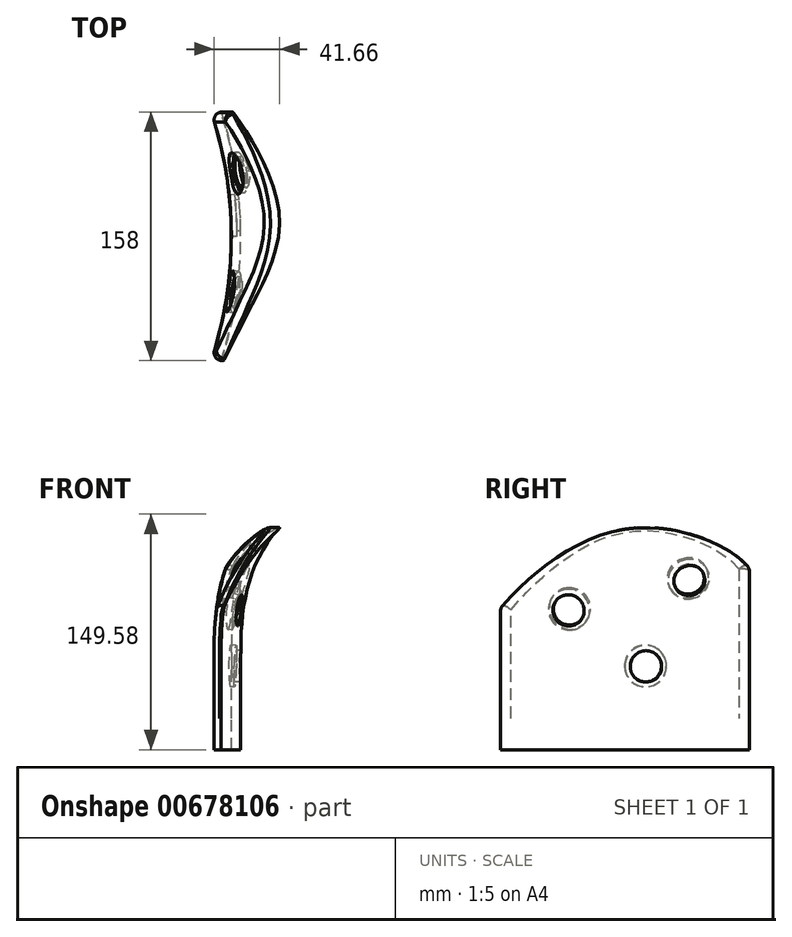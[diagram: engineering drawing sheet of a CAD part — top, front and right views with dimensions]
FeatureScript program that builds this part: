
annotation { "Feature Type Name" : "Feature", "Feature Type Description" : "" }
export const myFeature = defineFeature(function(context is Context, id is Id, definition is map)
    precondition{}
    {
        {
            var Q0;
            Q0=qCreatedBy(makeId("Top.planeOp"),FACE);
            var sketch = newSketch(context, id + "F0", { "sketchPlane" : qUnion([Q0])});
            skCircle(sketch, "E0", {"center": v(0, 0) * mm, "radius": 250 * mm});
            skCircle(sketch, "E1", {"center": v(0, 0) * mm, "radius": 256 * mm});
            skLineSegment(sketch, "E2", {"start": v(0, 0) * mm, "end": v(243.5, 79) * mm});
            skLineSegment(sketch, "E3", {"start": v(0, 0) * mm, "end": v(243.5, -79) * mm});
            skLineSegment(sketch, "E4", {"start": v(243.5, -79) * mm, "end": v(243.5, 79) * mm, "construction": true});
            skPoint(sketch, "E5", {"position": v(250, 0) * mm});
            skLineSegment(sketch, "E6", {"start": v(0, 0) * mm, "end": v(294.47, 0) * mm, "construction": true});
            skPoint(sketch, "E6.endSnap0", {"position": v(243.5, 0) * mm});
            skLineSegment(sketch, "E7", {"start": v(0, 0) * mm, "end": v(292.87, 46.39) * mm, "construction": true});
            skLineSegment(sketch, "E8", {"start": v(0, 0) * mm, "end": v(283.31, -39.82) * mm, "construction": true});
            skLineSegment(sketch, "E9", {"start": v(0, 0) * mm, "end": v(294.63, 15.44) * mm, "construction": true});
            skLineSegment(sketch, "E10", {"start": v(0, 0) * mm, "end": v(29.15, 207.44) * mm, "construction": true});
            skLineSegment(sketch, "E11", {"start": v(0, 0) * mm, "end": v(-10.87, 207.44) * mm, "construction": true});
            skLineSegment(sketch, "E12", {"start": v(0, 0) * mm, "end": v(-32.13, 202.88) * mm, "construction": true});
            skSolve(sketch);
        }
        {
            var Q0;
            Q0=qCreatedBy(makeId("Front.planeOp"),FACE);
            var sketch = newSketch(context, id + "F1", { "sketchPlane" : qUnion([Q0])});
            skLineSegment(sketch, "E13.0", {"start": v(-250, 0) * mm, "end": v(250, 0) * mm, "construction": true});
            skLineSegment(sketch, "E14.0", {"start": v(-256, 0) * mm, "end": v(256, 0) * mm, "construction": true});
            skPoint(sketch, "E15.0", {"position": v(243.5, 0) * mm});
            skLineSegment(sketch, "E16", {"start": v(250, 0) * mm, "end": v(256, 0) * mm, "construction": true});
            skPoint(sketch, "E17", {"position": v(253, 0) * mm});
            skFitSpline(sketch, "E18", {"points": [v(253, 0) * mm, v(253, 39.53) * mm, v(283, 127) * mm], "startDerivative": vector(0, 189.9) * mm, "endDerivative": vector(148.85, 126.61) * mm});
            skLineSegment(sketch, "E19", {"start": v(253, 0) * mm, "end": v(253, 133.7) * mm, "construction": true});
            skPoint(sketch, "E20", {"position": v(253, 66.85) * mm});
            skLineSegment(sketch, "E21", {"start": v(0, 0) * mm, "end": v(0, 247.7) * mm, "construction": true});
            skLineSegment(sketch, "E22", {"start": v(259.56, 90.88) * mm, "end": v(-13.45, 209.23) * mm, "construction": true});
            skLineSegment(sketch, "E23", {"start": v(0, 0) * mm, "end": v(70.48, 216.9) * mm, "construction": true});
            skLineSegment(sketch, "E24", {"start": v(0, 0) * mm, "end": v(46.92, 220.76) * mm, "construction": true});
            skLineSegment(sketch, "E25", {"start": v(0, 0) * mm, "end": v(14.68, 336.23) * mm, "construction": true});
            skSolve(sketch);
        }
        {
            var Q0;
            {var subQ0=sQuery(id+"F0.wireOp",EDGE,"E2");var subQ1=sQuery(id+"F0.wireOp",EDGE,"E0");var subQ2=makeQuery(id+"F0.imprint","INTERSECT",VERTEX,{"derivedFrom":[subQ1,subQ0]});Q0=makeQuery(id+"F0.imprint","IMPRINT",FACE,{"disambiguationData":[TD([[makeQuery(id+"F0.imprint","IMPRINT",EDGE,{"disambiguationData":[TD([[subQ2,1.0]])],"derivedFrom":subQ1}),-1.0]])]});}
            var Q1;
            Q1=sQuery(id+"F1.wireOp",EDGE,"E18");
            sweep(context, id + "F2", {"profiles" : qUnion([Q0]), "path" : qUnion([Q1])});
        }
        {
            var Q0;
            Q0=makeQuery(id+"F2.opSweep","SWEPT_EDGE",EDGE,{"disambiguationData":[OSD([sQuery(id+"F0.wireOp",EDGE,"E1"),sQuery(id+"F0.wireOp",EDGE,"E3"),sQuery(id+"F1.wireOp",EDGE,"E18")])]});
            cPoint(context, id + "F3", {"entities" : qUnion([Q0]), "parameter" : 0.5});
        }
        {
            var Q0;
            Q0=qCreatedBy(makeId("Front.planeOp"),FACE);
            var Q1;
            Q1=qCreatedBy(id+"F3",VERTEX);
            cPlane(context, id + "F4", {"entities" : qUnion([Q0, Q1]), "cplaneType" : CPlaneType.PLANE_POINT, "offset" : 25 * mm, "width" : 150 * mm, "height" : 150 * mm});
        }
        {
            var Q0;
            Q0=qCreatedBy(id+"F4.planeOp",FACE);
            var sketch = newSketch(context, id + "F5", { "sketchPlane" : qUnion([Q0])});
            skLineSegment(sketch, "E26", {"start": v(16.14, 70) * mm, "end": v(342.74, 70) * mm});
            skLineSegment(sketch, "E27.top", {"start": v(16.14, 220) * mm, "end": v(342.74, 220) * mm});
            skLineSegment(sketch, "E27.left", {"start": v(16.14, 70) * mm, "end": v(16.14, 220) * mm});
            skLineSegment(sketch, "E27.right", {"start": v(342.74, 70) * mm, "end": v(342.74, 220) * mm});
            skSolve(sketch);
        }
        {
            var Q0;
            Q0=qCreatedBy(makeId("Right.planeOp"),FACE);
            var sketch = newSketch(context, id + "F6", { "sketchPlane" : qUnion([Q0])});
            skPoint(sketch, "E28.0", {"position": v(-79, 70) * mm});
            skLineSegment(sketch, "E29", {"start": v(-74, 70) * mm, "end": v(-141.5, 70) * mm, "construction": true});
            skFitSpline(sketch, "E30.0", {"points": [v(74, 0) * mm, v(1000, 74) * mm, v(25.09, 1000) * mm, v(74, 37.34) * mm, v(1000, 74) * mm, v(48.67, 1000) * mm, v(74, 51.29) * mm, v(1000, 74) * mm, v(56.25, 1000) * mm, v(74, 58.58) * mm, v(1000, 74) * mm, v(63.15, 1000) * mm, v(74, 64.9) * mm, v(1000, 74) * mm, v(68.8, 1000) * mm, v(74, 70.94) * mm, v(1000, 74) * mm, v(77.76, 1000) * mm], "construction": true});
            skFitSpline(sketch, "E31.0", {"points": [v(-74, 0) * mm, v(1000, -74) * mm, v(25.09, 1000) * mm, v(-74, 37.34) * mm, v(1000, -74) * mm, v(48.67, 1000) * mm, v(-74, 51.29) * mm, v(1000, -74) * mm, v(56.25, 1000) * mm, v(-74, 58.58) * mm, v(1000, -74) * mm, v(63.15, 1000) * mm, v(-74, 64.9) * mm, v(1000, -74) * mm, v(68.8, 1000) * mm, v(-74, 70.94) * mm, v(1000, -74) * mm, v(77.76, 1000) * mm], "construction": true});
            skLineSegment(sketch, "E32", {"start": v(68.45, 95) * mm, "end": v(-5.43, 95) * mm, "construction": true});
            skLineSegment(sketch, "E33", {"start": v(28.07, 120) * mm, "end": v(-24.08, 120) * mm, "construction": true});
            skFitSpline(sketch, "E34", {"points": [v(79, 95) * mm, v(37.6, 117.94) * mm, v(0, 120) * mm, v(-31.96, 108.87) * mm, v(-79, 70) * mm], "startDerivative": vector(-101.15, 130.6) * mm, "endDerivative": vector(-145.98, -173.37) * mm});
            skSolve(sketch);
        }
        {
            var Q0;
            Q0=makeQuery(id+"F5.imprint","IMPRINT",FACE,{"disambiguationData":[TD([[makeQuery(id+"F5.imprint","IMPRINT",EDGE,{"derivedFrom":sQuery(id+"F5.wireOp",EDGE,"E26")}),1.0]])]});
            var Q1;
            Q1=sQuery(id+"F6.wireOp",EDGE,"E34");
            sweep(context, id + "F7", {"operationType" : NewBodyOperationType.REMOVE, "profiles" : qUnion([Q0]), "path" : qUnion([Q1]), "keepProfileOrientation" : true});
        }
        {
            var Q0;
            Q0=makeQuery(id+"F7.boolean.opBoolean","INTERSECT",EDGE,{"derivedFrom":[makeQuery(id+"F2.opSweep","SWEPT_FACE",FACE,{"disambiguationData":[OSD([sQuery(id+"F0.wireOp",EDGE,"E0"),sQuery(id+"F1.wireOp",EDGE,"E18")])]}),makeQuery(id+"F7.opSweep","SWEPT_FACE",FACE,{"disambiguationData":[OSD([sQuery(id+"F5.wireOp",EDGE,"E26"),sQuery(id+"F6.wireOp",EDGE,"E34")])]})]});
            fillet(context, id + "F8", {"entities" : qUnion([Q0]), "radius" : 5 * mm, "tangentPropagation" : true, "allowEdgeOverflow" : false});
        }
        {
            var Q0;
            Q0=makeQuery(id+"F2.opSweep","SWEPT_EDGE",EDGE,{"disambiguationData":[OSD([sQuery(id+"F0.wireOp",EDGE,"E0"),sQuery(id+"F0.wireOp",EDGE,"E2"),sQuery(id+"F1.wireOp",EDGE,"E18")])]});
            var Q1;
            Q1=makeQuery(id+"F2.opSweep","SWEPT_EDGE",EDGE,{"disambiguationData":[OSD([sQuery(id+"F0.wireOp",EDGE,"E0"),sQuery(id+"F0.wireOp",EDGE,"E3"),sQuery(id+"F1.wireOp",EDGE,"E18")])]});
            fillet(context, id + "F9", {"entities" : qUnion([Q0, Q1]), "radius" : 5 * mm, "tangentPropagation" : true, "allowEdgeOverflow" : false});
        }
        {
            var Q0;
            Q0=makeQuery(id+"F2.opSweep","CAP_FACE",FACE,{"disambiguationData":[OSD([sQuery(id+"F0.wireOp",EDGE,"E0"),sQuery(id+"F0.wireOp",EDGE,"E1"),sQuery(id+"F0.wireOp",EDGE,"E2"),sQuery(id+"F0.wireOp",EDGE,"E3"),sQuery(id+"F1.wireOp",VERTEX,"E18.start")])],"isStart":true});
            var sketch = newSketch(context, id + "F10", { "sketchPlane" : qUnion([Q0])});
            skLineSegment(sketch, "E35.0.0", {"start": v(243.5, 79) * mm, "end": v(242.5, 78.68) * mm});
            skArc(sketch, "E35.0.1", {"start": v(242.5, 78.68) * mm, "mid": v(239.62, 76.24) * mm, "end": v(239.27, 72.47) * mm});
            skArc(sketch, "E35.0.2", {"start": v(239.27, -72.47) * mm, "mid": v(250, 0) * mm, "end": v(239.27, 72.47) * mm});
            skArc(sketch, "E35.0.3", {"start": v(239.27, -72.47) * mm, "mid": v(239.62, -76.24) * mm, "end": v(242.5, -78.68) * mm});
            skLineSegment(sketch, "E35.0.4", {"start": v(243.5, -79) * mm, "end": v(242.5, -78.68) * mm});
            skArc(sketch, "E35.0.5", {"start": v(243.5, -79) * mm, "mid": v(256, 0) * mm, "end": v(243.5, 79) * mm});
            skSolve(sketch);
        }
        {
            var Q0;
            Q0=makeQuery(id+"F10.imprint","IMPRINT",FACE,{"disambiguationData":[TD([[makeQuery(id+"F10.imprint","IMPRINT",EDGE,{"derivedFrom":sQuery(id+"F10.wireOp",EDGE,"E35.0.0")}),-1.0]])]});
            extrude(context, id + "F11", {"entities" : qUnion([Q0]), "operationType" : NewBodyOperationType.ADD, "depth" : 20 * mm, "offsetDistance" : 25 * mm});
        }
        {
            var Q0;
            Q0=sQuery(id+"F0.wireOp",VERTEX,"E12.end");
            var Q1;
            Q1=sQuery(id+"F0.wireOp",VERTEX,"E2.start");
            var Q2;
            Q2=sQuery(id+"F1.wireOp",VERTEX,"E23.end");
            cPlane(context, id + "F12", {"entities" : qUnion([Q0, Q1, Q2]), "cplaneType" : CPlaneType.THREE_POINT, "offset" : 25 * mm, "width" : 150 * mm, "height" : 150 * mm});
        }
        {
            var Q0;
            Q0=qCreatedBy(id+"F12.planeOp",FACE);
            var sketch = newSketch(context, id + "F13", { "sketchPlane" : qUnion([Q0])});
            skLineSegment(sketch, "E36.0", {"start": v(0, 0) * mm, "end": v(4.38, 90.5) * mm, "construction": true});
            skCircle(sketch, "E37", {"center": v(7.89, 163) * mm, "radius": 10 * mm});
            skCircle(sketch, "E38", {"center": v(7.89, 163) * mm, "radius": 13.25 * mm});
            skSolve(sketch);
        }
        {
            var Q0;
            Q0=makeQuery(id+"F13.imprint","IMPRINT",FACE,{"disambiguationData":[TD([[makeQuery(id+"F13.imprint","IMPRINT",EDGE,{"derivedFrom":sQuery(id+"F13.wireOp",EDGE,"E37")}),1.0]])]});
            var Q1;
            Q1=makeQuery(id+"F2.opSweep","SWEPT_BODY",BODY,{"disambiguationData":[OSD([sQuery(id+"F0.wireOp",EDGE,"E0"),sQuery(id+"F0.wireOp",EDGE,"E1"),sQuery(id+"F0.wireOp",EDGE,"E2"),sQuery(id+"F0.wireOp",EDGE,"E3"),sQuery(id+"F1.wireOp",EDGE,"E18")])]});
            extrude(context, id + "F14", {"entities" : qUnion([Q0]), "operationType" : NewBodyOperationType.REMOVE, "endBound" : BoundingType.UP_TO_BODY, "depth" : 25 * mm, "endBoundEntityBody" : qUnion([Q1]), "hasOffset" : true, "offsetDistance" : 10 * mm, "offsetOppositeDirection" : true});
        }
        {
            var Q0;
            Q0=makeQuery(id+"F13.imprint","IMPRINT",FACE,{"disambiguationData":[TD([[makeQuery(id+"F13.imprint","IMPRINT",EDGE,{"derivedFrom":sQuery(id+"F13.wireOp",EDGE,"E37")}),-1.0]])]});
            extrude(context, id + "F15", {"entities" : qUnion([Q0]), "operationType" : NewBodyOperationType.REMOVE, "depth" : (215.5 + 4) * mm, "offsetDistance" : 25 * mm});
        }
        {
            var Q0;
            Q0=sQuery(id+"F0.wireOp",VERTEX,"E10.end");
            var Q1;
            Q1=sQuery(id+"F0.wireOp",VERTEX,"E2.start");
            var Q2;
            Q2=sQuery(id+"F1.wireOp",VERTEX,"E24.end");
            cPlane(context, id + "F16", {"entities" : qUnion([Q0, Q1, Q2]), "cplaneType" : CPlaneType.THREE_POINT, "offset" : 25 * mm, "width" : 150 * mm, "height" : 150 * mm});
        }
        {
            var Q0;
            Q0=qCreatedBy(id+"F16.planeOp",FACE);
            var sketch = newSketch(context, id + "F17", { "sketchPlane" : qUnion([Q0])});
            skLineSegment(sketch, "E39.0", {"start": v(0, 0) * mm, "end": v(-1.7, 58.9) * mm, "construction": true});
            skCircle(sketch, "E40", {"center": v(-3.47, 120) * mm, "radius": 10 * mm});
            skCircle(sketch, "E41", {"center": v(-3.47, 120) * mm, "radius": 13.25 * mm});
            skSolve(sketch);
        }
        {
            var Q0;
            Q0=makeQuery(id+"F17.imprint","IMPRINT",FACE,{"disambiguationData":[TD([[makeQuery(id+"F17.imprint","IMPRINT",EDGE,{"derivedFrom":sQuery(id+"F17.wireOp",EDGE,"E40")}),1.0]])]});
            var Q1;
            Q1=makeQuery(id+"F2.opSweep","SWEPT_BODY",BODY,{"disambiguationData":[OSD([sQuery(id+"F0.wireOp",EDGE,"E0"),sQuery(id+"F0.wireOp",EDGE,"E1"),sQuery(id+"F0.wireOp",EDGE,"E2"),sQuery(id+"F0.wireOp",EDGE,"E3"),sQuery(id+"F1.wireOp",EDGE,"E18")])]});
            extrude(context, id + "F18", {"entities" : qUnion([Q0]), "operationType" : NewBodyOperationType.REMOVE, "endBound" : BoundingType.UP_TO_BODY, "depth" : 25 * mm, "endBoundEntityBody" : qUnion([Q1]), "hasOffset" : true, "offsetDistance" : 10 * mm, "offsetOppositeDirection" : true});
        }
        {
            var Q0;
            Q0=makeQuery(id+"F17.imprint","IMPRINT",FACE,{"disambiguationData":[TD([[makeQuery(id+"F17.imprint","IMPRINT",EDGE,{"derivedFrom":sQuery(id+"F17.wireOp",EDGE,"E40")}),-1.0]])]});
            extrude(context, id + "F19", {"entities" : qUnion([Q0]), "operationType" : NewBodyOperationType.REMOVE, "depth" : (231.6 + 4) * mm, "offsetDistance" : 25 * mm});
        }
        {
            var Q0;
            Q0=sQuery(id+"F0.wireOp",VERTEX,"E11.end");
            var Q1;
            Q1=sQuery(id+"F0.wireOp",VERTEX,"E2.start");
            var Q2;
            Q2=sQuery(id+"F1.wireOp",VERTEX,"E25.end");
            cPlane(context, id + "F20", {"entities" : qUnion([Q0, Q1, Q2]), "cplaneType" : CPlaneType.THREE_POINT, "offset" : 25 * mm, "width" : 150 * mm, "height" : 150 * mm});
        }
        {
            var Q0;
            Q0=qCreatedBy(id+"F20.planeOp",FACE);
            var sketch = newSketch(context, id + "F21", { "sketchPlane" : qUnion([Q0])});
            skLineSegment(sketch, "E42.0", {"start": v(0, 0) * mm, "end": v(0.03, 12.85) * mm, "construction": true});
            skLineSegment(sketch, "E43", {"start": v(0.03, 12.85) * mm, "end": v(0.03, 95.77) * mm, "construction": true});
            skCircle(sketch, "E44", {"center": v(0.03, 44) * mm, "radius": 10 * mm});
            skCircle(sketch, "E45", {"center": v(0.03, 44) * mm, "radius": 13.25 * mm});
            skSolve(sketch);
        }
        {
            var Q0;
            Q0=makeQuery(id+"F21.imprint","IMPRINT",FACE,{"disambiguationData":[TD([[makeQuery(id+"F21.imprint","IMPRINT",EDGE,{"derivedFrom":sQuery(id+"F21.wireOp",EDGE,"E44")}),1.0]])]});
            var Q1;
            Q1=makeQuery(id+"F2.opSweep","SWEPT_BODY",BODY,{"disambiguationData":[OSD([sQuery(id+"F0.wireOp",EDGE,"E0"),sQuery(id+"F0.wireOp",EDGE,"E1"),sQuery(id+"F0.wireOp",EDGE,"E2"),sQuery(id+"F0.wireOp",EDGE,"E3"),sQuery(id+"F1.wireOp",EDGE,"E18")])]});
            extrude(context, id + "F22", {"entities" : qUnion([Q0]), "operationType" : NewBodyOperationType.REMOVE, "endBound" : BoundingType.UP_TO_BODY, "depth" : 25 * mm, "endBoundEntityBody" : qUnion([Q1]), "hasOffset" : true, "offsetDistance" : 10 * mm, "offsetOppositeDirection" : true});
        }
        {
            var Q0;
            Q0=makeQuery(id+"F21.imprint","IMPRINT",FACE,{"disambiguationData":[TD([[makeQuery(id+"F21.imprint","IMPRINT",EDGE,{"derivedFrom":sQuery(id+"F21.wireOp",EDGE,"E44")}),-1.0]])]});
            extrude(context, id + "F23", {"entities" : qUnion([Q0]), "operationType" : NewBodyOperationType.REMOVE, "depth" : (247.2 + 4) * mm, "offsetDistance" : 25 * mm});
        }
    });
